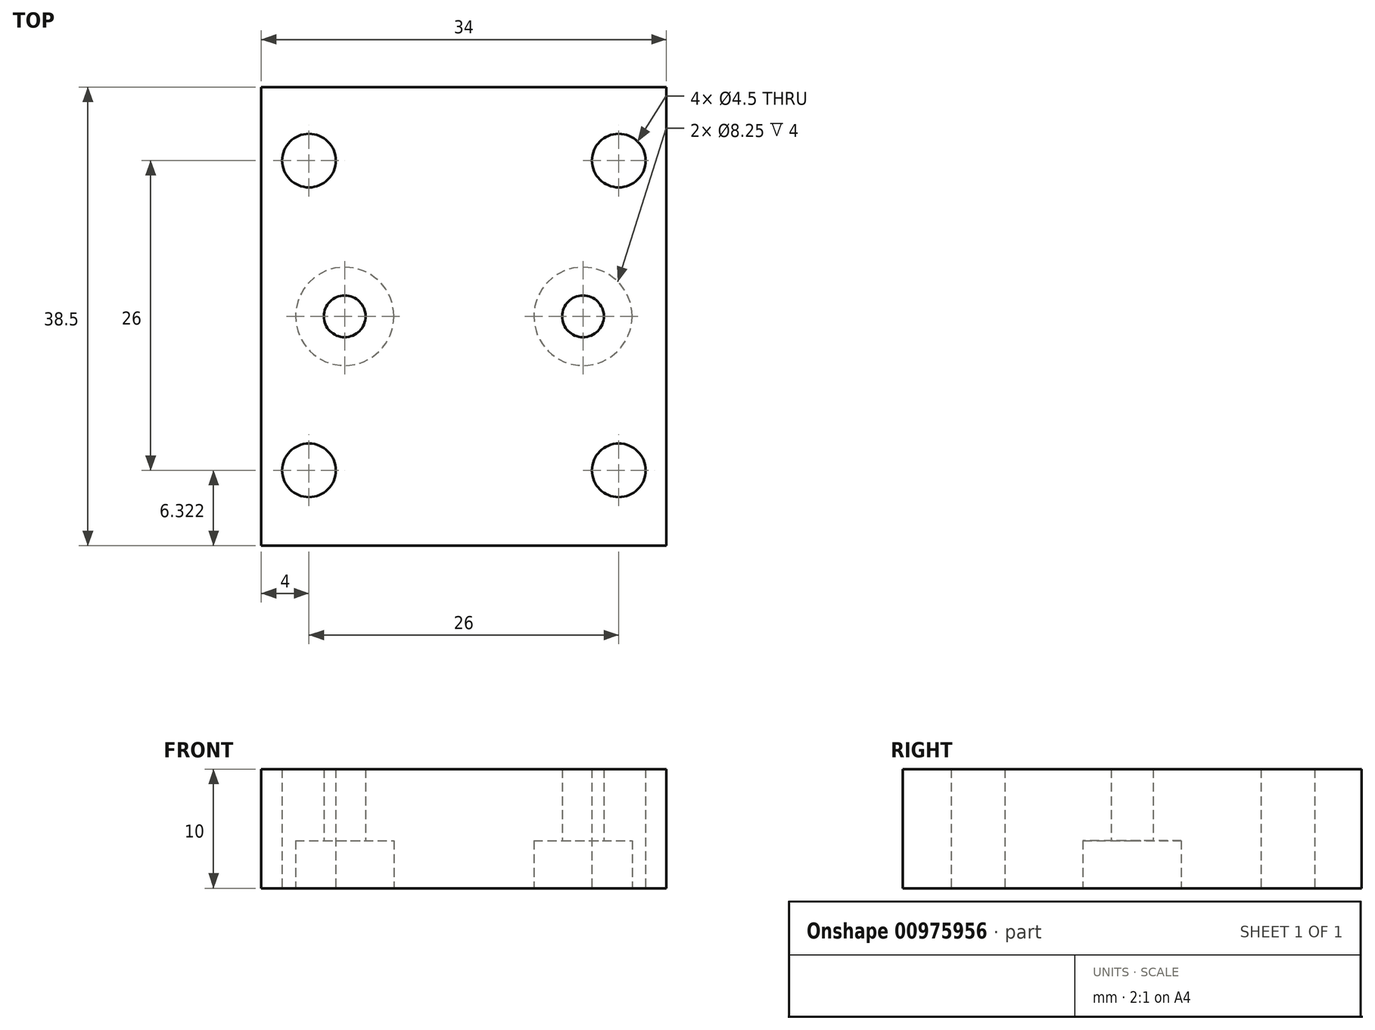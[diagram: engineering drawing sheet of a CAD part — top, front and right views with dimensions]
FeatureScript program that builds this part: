
annotation { "Feature Type Name" : "Feature", "Feature Type Description" : "" }
export const myFeature = defineFeature(function(context is Context, id is Id, definition is map)
    precondition{}
    {
        {
            var Q0;
            Q0=qCreatedBy(makeId("Top.planeOp"),FACE);
            var sketch = newSketch(context, id + "F0", { "sketchPlane" : qUnion([Q0])});
            skLineSegment(sketch, "E0.bottom", {"start": v(17, -19.25) * mm, "end": v(-17, -19.25) * mm});
            skLineSegment(sketch, "E0.top", {"start": v(17, 19.25) * mm, "end": v(-17, 19.25) * mm});
            skLineSegment(sketch, "E0.left", {"start": v(17, -19.25) * mm, "end": v(17, 19.25) * mm});
            skLineSegment(sketch, "E0.right", {"start": v(-17, -19.25) * mm, "end": v(-17, 19.25) * mm});
            skPoint(sketch, "E0.middle", {"position": v(0, 0) * mm});
            skSolve(sketch);
        }
        {
            var Q0;
            Q0=makeQuery(id+"F0.imprint","IMPRINT",FACE,{"disambiguationData":[TD([[makeQuery(id+"F0.imprint","IMPRINT",EDGE,{"derivedFrom":sQuery(id+"F0.wireOp",EDGE,"E0.bottom")}),-1.0]])]});
            extrude(context, id + "F1", {"entities" : qUnion([Q0]), "depth" : 10 * mm, "offsetDistance" : 25 * mm});
        }
        {
            var Q0;
            Q0=makeQuery(id+"F1.opExtrude","CAP_FACE",FACE,{"disambiguationData":[OSD([sQuery(id+"F0.wireOp",EDGE,"E0.bottom"),sQuery(id+"F0.wireOp",EDGE,"E0.top"),sQuery(id+"F0.wireOp",EDGE,"E0.left"),sQuery(id+"F0.wireOp",EDGE,"E0.right")])],"isStart":true});
            var sketch = newSketch(context, id + "F2", { "sketchPlane" : qUnion([Q0])});
            skPoint(sketch, "E1", {"position": v(-13, 12.93) * mm});
            skPoint(sketch, "E2", {"position": v(-13, -13.07) * mm});
            skPoint(sketch, "E3.MirrorP", {"position": v(13, 12.93) * mm});
            skPoint(sketch, "E4.MirrorP", {"position": v(13, -13.07) * mm});
            skSolve(sketch);
        }
        {
            var Q0;
            Q0=sQuery(id+"F2.wireOp",VERTEX,"E1");
            var Q1;
            Q1=sQuery(id+"F2.wireOp",VERTEX,"E3.MirrorP");
            var Q2;
            Q2=sQuery(id+"F2.wireOp",VERTEX,"E2");
            var Q3;
            Q3=sQuery(id+"F2.wireOp",VERTEX,"E4.MirrorP");
            var Q4;
            Q4=makeQuery(id+"F1.opExtrude","SWEPT_BODY",BODY,{"disambiguationData":[OSD([sQuery(id+"F0.wireOp",EDGE,"E0.bottom"),sQuery(id+"F0.wireOp",EDGE,"E0.top"),sQuery(id+"F0.wireOp",EDGE,"E0.left"),sQuery(id+"F0.wireOp",EDGE,"E0.right")])]});
            hole(context, id + "F3", {"style" : HoleStyle.SIMPLE, "endStyle" : HoleEndStyle.BLIND, "standardTappedOrClearance" : lookupTablePath({ "fit" : "Normal", "standard" : "ISO", "size" : "M4", "type" : "Clearance" }), "standardBlindInLast" : lookupTablePath({ "fit" : "Normal", "standard" : "ISO", "engagement" : "75%", "pitch" : "0.7 mm", "size" : "M4", "type" : "Clearance & tapped" }), "holeDiameter" : 4.5 * mm, "majorDiameter" : 5 * mm, "holeDepth" : 10 * mm, "isTappedThrough" : true, "tappedDepth" : 10 * mm, "tapClearance" : 3, "locations" : qUnion([Q0, Q1, Q2, Q3]), "scope" : qUnion([Q4])});
        }
        {
            var Q0;
            Q0=makeQuery(id+"F1.opExtrude","CAP_FACE",FACE,{"disambiguationData":[OSD([sQuery(id+"F0.wireOp",EDGE,"E0.bottom"),sQuery(id+"F0.wireOp",EDGE,"E0.top"),sQuery(id+"F0.wireOp",EDGE,"E0.left"),sQuery(id+"F0.wireOp",EDGE,"E0.right")])],"isStart":true});
            var sketch = newSketch(context, id + "F4", { "sketchPlane" : qUnion([Q0])});
            skLineSegment(sketch, "E5", {"start": v(17, 0) * mm, "end": v(-17, 0) * mm});
            skPoint(sketch, "E6", {"position": v(10, 0) * mm});
            skPoint(sketch, "E7", {"position": v(-10, 0) * mm});
            skSolve(sketch);
        }
        {
            var Q0;
            Q0=sQuery(id+"F4.wireOp",VERTEX,"E6");
            var Q1;
            Q1=sQuery(id+"F4.wireOp",VERTEX,"E7");
            var Q2;
            Q2=makeQuery(id+"F1.opExtrude","SWEPT_BODY",BODY,{"disambiguationData":[OSD([sQuery(id+"F0.wireOp",EDGE,"E0.bottom"),sQuery(id+"F0.wireOp",EDGE,"E0.top"),sQuery(id+"F0.wireOp",EDGE,"E0.left"),sQuery(id+"F0.wireOp",EDGE,"E0.right")])]});
            hole(context, id + "F5", {"style" : HoleStyle.C_BORE, "endStyle" : HoleEndStyle.BLIND, "standardTappedOrClearance" : lookupTablePath({ "standard" : "ISO", "engagement" : "75%", "pitch" : "0.5 mm", "size" : "M4", "type" : "Tapped" }), "standardBlindInLast" : lookupTablePath({ "standard" : "ISO", "fit" : "Normal", "engagement" : "75%", "pitch" : "0.5 mm", "size" : "M4", "type" : "Clearance & tapped" }), "holeDiameter" : 3.5 * mm, "cBoreDiameter" : 8.25 * mm, "cBoreDepth" : 4 * mm, "majorDiameter" : 4 * mm, "showTappedDepth" : true, "holeDepth" : 10 * mm, "isTappedThrough" : true, "tappedDepth" : 9 * mm, "tapClearance" : 2, "locations" : qUnion([Q0, Q1]), "scope" : qUnion([Q2])});
        }
    });
